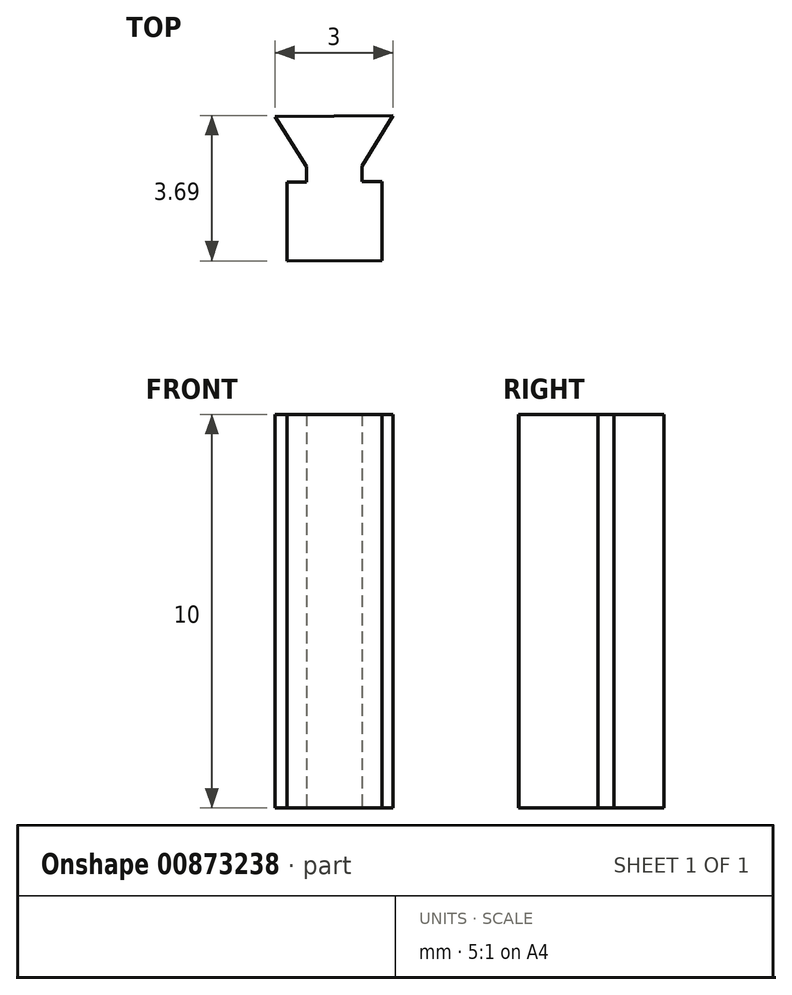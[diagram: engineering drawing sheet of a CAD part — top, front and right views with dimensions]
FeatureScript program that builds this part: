
annotation { "Feature Type Name" : "Feature", "Feature Type Description" : "" }
export const myFeature = defineFeature(function(context is Context, id is Id, definition is map)
    precondition{}
    {
        {
            var Q0;
            Q0=qCreatedBy(makeId("Top.planeOp"),FACE);
            var sketch = newSketch(context, id + "F0", { "sketchPlane" : qUnion([Q0])});
            skLineSegment(sketch, "E0", {"start": v(-6.66, -11.25) * mm, "end": v(-9.66, -11.28) * mm});
            skLineSegment(sketch, "E1", {"start": v(-7.44, -12.53) * mm, "end": v(-6.66, -11.25) * mm});
            skLineSegment(sketch, "E2", {"start": v(-9.66, -11.28) * mm, "end": v(-8.85, -12.54) * mm});
            skLineSegment(sketch, "E3", {"start": v(-7.44, -12.53) * mm, "end": v(-7.44, -12.93) * mm});
            skLineSegment(sketch, "E4", {"start": v(-7.44, -12.93) * mm, "end": v(-6.94, -12.93) * mm});
            skLineSegment(sketch, "E5", {"start": v(-6.94, -12.93) * mm, "end": v(-6.94, -14.93) * mm});
            skLineSegment(sketch, "E6", {"start": v(-8.85, -12.54) * mm, "end": v(-8.85, -12.94) * mm});
            skLineSegment(sketch, "E7", {"start": v(-8.85, -12.94) * mm, "end": v(-9.35, -12.94) * mm});
            skLineSegment(sketch, "E8", {"start": v(-9.35, -12.94) * mm, "end": v(-9.35, -14.94) * mm});
            skLineSegment(sketch, "E9", {"start": v(-9.35, -14.94) * mm, "end": v(-6.94, -14.93) * mm});
            skSolve(sketch);
        }
        {
            var Q0;
            Q0=makeQuery(id+"F0.imprint","IMPRINT",FACE,{"disambiguationData":[TD([[makeQuery(id+"F0.imprint","IMPRINT",EDGE,{"derivedFrom":sQuery(id+"F0.wireOp",EDGE,"E0")}),1.0]])]});
            extrude(context, id + "F1", {"entities" : qUnion([Q0]), "depth" : 10 * mm, "offsetDistance" : 25 * mm});
        }
    });
